# Revit family: Hager-UNIVERS-Surface_mounted-IP30-Without_Cover-With_DIN-Hosted-CH-it
name_source: partatom
category: Electrical Equipment
units: mm (PartAtom-declared; Revit-internal decimal feet)

## family parameters
Cut with Voids When Loaded = No
Host = Face
Maintain Annotation Orientation = Yes
Panel Configuration = Two Columns, Circuits Across
Part Type = Panelboard
Room Calculation Point = No
Round Connector Dimension = Use Diameter
Shared = No

## types (20) — shared parameters
BC_MODEL_ID = 1539164
BC_OBJECT_ID = 512278
BC_OBJECT_VERSION = #40
Code hager = ADD-EC000214_EU
EF000003 - modo di montaggio = apparente/incassato
EF000007 - colore = bianco
EF000024 - resistente ai raggi UV = No
EF000049 - profondità = 165 mm  [stored 0.541339 ft]
EF000116 - numero RAL = 9010
EF000118 - con piastra di montaggio = No
EF000218 - profondità di montaggio = 161 mm  [stored 0.528215 ft]
EF001062 - versione EMC = No
EF001088 - possibilità di applicazione = Yes
EF001134 - barra DIN = Yes
EF004462 - tipo di chiusura = altri
EF005474 - grado di protezione (IP) = IP30
EF006244 - coperchio/porta trasparente = No
EF006306 - con serratura = No
EF009212 - tipo di coperchio = con taglio
EF015776 - morsetto di messa a terra = Yes
EF015777 - morsettiera a conduttore neutro = Yes
EF015941 - porta di trasmissione del segnale = No
ETIM class code = EC000214
ETIM class name = Small distribution board
HG000002-with door or cover-it = No
HG000003-Range-it = UNIVERS
HG000005-Thickness-it = 2 mm  [stored 0.00656168 ft]
HG000006-Flush mounted-it = No
HG000009-Double swing door-it = No
HG000010-Asymmetric doors-it = No
HG000011-Empty rows from bottom-it = No
HG000012-Door swing angle-it = 90.00°
HG000013-Door on the left-it = No
HG000014-Door on the right-it = Yes
HG000015-Clearance visibility-it = Yes
HG000016-Door 3D visibility-it = Yes
HG000017-Distance between poles-it = 18 mm  [stored 0.0590551 ft]
HG000060-RAL-number = 9010
HG000099-Onfly Template ID-it-CH = 507532
Manufacturer = Hager
Name = Hager-UNIVERS-Surface_mounted-IP30-Without_Cover-With_DIN-NoHosted-CH-it
Name BIM&CO = Electricity
Name hager = ADD_Enclosures_EC000214
Uniformat = Low Tension Service & Dist.
Uniformat code = D501001
zero-valued in all types: Default Elevation, EF001131 - profondità interna, HG000007-Number of empty columns-it, HG000008-Number of empty rows-it

## per-type parameters (varying)
| type | BC_VARIANT_ID | EF000008 - larghezza | EF000040 - altezza | EF000266 - numero di file | EF000332 - altezza di installazione | EF000846 - larghezza di montaggio | EF002950 - numero di unità modulari | HG000001 - Numero di colonne | HG000004-Manufacturer reference-it | HGEF000266-Numero di file | HGEF0002950-larghezza in unità di suddivisione |
| UNIVERS-Surface_mounted_W300_H500_D165_12_Modular_Spacing-FWB31T1S | 1169520 | 300 mm | 500 mm  [stored 1.64042 ft] | 3 | 500 mm  [stored 1.64042 ft] | 300 mm | 12 | 1 | FWB31T1S | 3 | 12 |
| UNIVERS-Surface_mounted_W550_H500_D165_24_Modular_Spacing-FWB32T1S | 1169521 | 550 mm | 500 mm  [stored 1.64042 ft] | 3 | 500 mm  [stored 1.64042 ft] | 550 mm | 24 | 2 | FWB32T1S | 3 | 24 |
| UNIVERS-Surface_mounted_W800_H500_D165_36_Modular_Spacing-FWB33T1S | 1169522 | 800 mm  [stored 2.62467 ft] | 500 mm  [stored 1.64042 ft] | 3 | 500 mm  [stored 1.64042 ft] | 800 mm  [stored 2.62467 ft] | 36 | 3 | FWB33T1S | 3 | 36 |
| UNIVERS-Surface_mounted_W1050_H500_D165_48_Modular_Spacing-FWB34T1S | 1169523 | 1050 mm | 500 mm  [stored 1.64042 ft] | 3 | 500 mm  [stored 1.64042 ft] | 1050 mm | 48 | 4 | FWB34T1S | 3 | 48 |
| UNIVERS-Surface_mounted_W300_H650_D165_12_Modular_Spacing-FWB41T1S | 1169524 | 300 mm | 650 mm  [stored 2.13255 ft] | 4 | 650 mm  [stored 2.13255 ft] | 300 mm | 12 | 1 | FWB41T1S | 4 | 12 |
| UNIVERS-Surface_mounted_W550_H650_D165_24_Modular_Spacing-FWB42T1S | 1169525 | 550 mm | 650 mm  [stored 2.13255 ft] | 4 | 650 mm  [stored 2.13255 ft] | 550 mm | 24 | 2 | FWB42T1S | 4 | 24 |
| UNIVERS-Surface_mounted_W800_H650_D165_36_Modular_Spacing-FWB43T1S | 1169526 | 800 mm  [stored 2.62467 ft] | 650 mm  [stored 2.13255 ft] | 4 | 650 mm  [stored 2.13255 ft] | 800 mm  [stored 2.62467 ft] | 36 | 3 | FWB43T1S | 4 | 36 |
| UNIVERS-Surface_mounted_W1050_H650_D165_48_Modular_Spacing-FWB44T1S | 1169527 | 1050 mm | 650 mm  [stored 2.13255 ft] | 4 | 650 mm  [stored 2.13255 ft] | 1050 mm | 48 | 4 | FWB44T1S | 4 | 48 |
| UNIVERS-Surface_mounted_W300_H800_D165_12_Modular_Spacing-FWB51T1S | 1169528 | 300 mm | 800 mm  [stored 2.62467 ft] | 5 | 800 mm  [stored 2.62467 ft] | 300 mm | 12 | 1 | FWB51T1S | 5 | 12 |
| UNIVERS-Surface_mounted_W550_H800_D165_24_Modular_Spacing-FWB52T1S | 1169529 | 550 mm | 800 mm  [stored 2.62467 ft] | 5 | 800 mm  [stored 2.62467 ft] | 550 mm | 24 | 2 | FWB52T1S | 5 | 24 |
| UNIVERS-Surface_mounted_W800_H800_D165_36_Modular_Spacing-FWB53T1S | 1169530 | 800 mm  [stored 2.62467 ft] | 800 mm  [stored 2.62467 ft] | 5 | 800 mm  [stored 2.62467 ft] | 800 mm  [stored 2.62467 ft] | 36 | 3 | FWB53T1S | 5 | 36 |
| UNIVERS-Surface_mounted_W1050_H800_D165_48_Modular_Spacing-FWB54T1S | 1169531 | 1050 mm | 800 mm  [stored 2.62467 ft] | 5 | 800 mm  [stored 2.62467 ft] | 1050 mm | 48 | 4 | FWB54T1S | 5 | 48 |
| UNIVERS-Surface_mounted_W300_H950_D165_12_Modular_Spacing-FWB61T1S | 1169532 | 300 mm | 950 mm  [stored 3.1168 ft] | 6 | 950 mm  [stored 3.1168 ft] | 300 mm | 12 | 1 | FWB61T1S | 6 | 12 |
| UNIVERS-Surface_mounted_W550_H950_D165_24_Modular_Spacing-FWB62T1S | 1169535 | 550 mm | 950 mm  [stored 3.1168 ft] | 6 | 950 mm  [stored 3.1168 ft] | 550 mm | 24 | 2 | FWB62T1S | 6 | 24 |
| UNIVERS-Surface_mounted_W800_H950_D165_36_Modular_Spacing-FWB63T1S | 1169544 | 800 mm  [stored 2.62467 ft] | 950 mm  [stored 3.1168 ft] | 6 | 950 mm  [stored 3.1168 ft] | 800 mm  [stored 2.62467 ft] | 36 | 3 | FWB63T1S | 6 | 36 |
| UNIVERS-Surface_mounted_W1050_H950_D165_48_Modular_Spacing-FWB64T1S | 1169550 | 1050 mm | 950 mm  [stored 3.1168 ft] | 6 | 950 mm  [stored 3.1168 ft] | 1050 mm | 48 | 4 | FWB64T1S | 6 | 48 |
| UNIVERS-Surface_mounted_W300_H1100_D165_12_Modular_Spacing-FWB71T1S | 1169559 | 300 mm | 1100 mm | 7 | 1100 mm | 300 mm | 12 | 1 | FWB71T1S | 7 | 12 |
| UNIVERS-Surface_mounted_W550_H1100_D165_24_Modular_Spacing-FWB72T1S | 1169568 | 550 mm | 1100 mm | 7 | 1100 mm | 550 mm | 24 | 2 | FWB72T1S | 7 | 24 |
| UNIVERS-Surface_mounted_W800_H1100_D165_36_Modular_Spacing-FWB73T1S | 1169576 | 800 mm  [stored 2.62467 ft] | 1100 mm | 7 | 1100 mm | 800 mm  [stored 2.62467 ft] | 36 | 3 | FWB73T1S | 7 | 36 |
| UNIVERS-Surface_mounted_W1050_H1100_D165_48_Modular_Spacing-FWB74T1S | 1169586 | 1050 mm | 1100 mm | 7 | 1100 mm | 1050 mm | 48 | 4 | FWB74T1S | 7 | 48 |

note: column(s) folded — value = type name in every type: Reference

note: [stored X ft] marks values corroborated as IEEE doubles in the binary element streams (Revit-internal decimal feet)

## geometry (parser evidence)
native form markers: Sweep x16
no freeform markers — native parametric forms only
